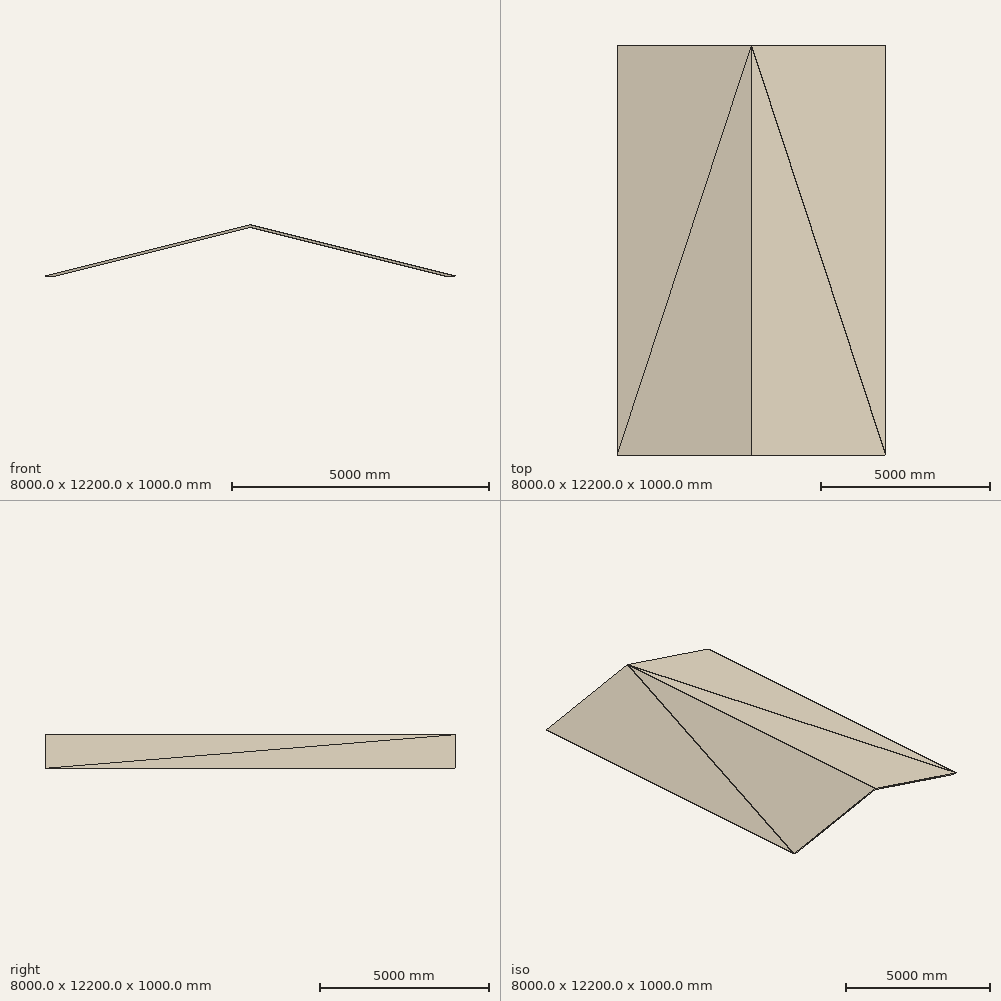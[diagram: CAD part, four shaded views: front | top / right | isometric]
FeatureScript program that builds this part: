
annotation { "Feature Type Name" : "Feature", "Feature Type Description" : "" }
export const myFeature = defineFeature(function(context is Context, id is Id, definition is map)
    precondition{}
    {
        {
            var Q0;
            Q0=qCreatedBy(makeId("Front.planeOp"),FACE);
            var sketch = newSketch(context, id + "F0", { "sketchPlane" : qUnion([Q0])});
            skLineSegment(sketch, "E0", {"start": v(0, 0) * mm, "end": v(8000, 0) * mm, "construction": true});
            skLineSegment(sketch, "E1", {"start": v(8000, 0) * mm, "end": v(4000, 1000) * mm});
            skLineSegment(sketch, "E2", {"start": v(4000, 1000) * mm, "end": v(0, 0) * mm});
            skLineSegment(sketch, "E3", {"start": v(0, 0) * mm, "end": v(206.16, 0) * mm});
            skLineSegment(sketch, "E4", {"start": v(206.16, 0) * mm, "end": v(4000, 948.46) * mm});
            skLineSegment(sketch, "E5", {"start": v(4000, 948.46) * mm, "end": v(7793.84, 0) * mm});
            skLineSegment(sketch, "E6", {"start": v(7793.84, 0) * mm, "end": v(8000, 0) * mm});
            skSolve(sketch);
        }
        {
            var Q0;
            Q0 = qSketchRegion(id + "F0", true);
            extrude(context, id + "F1", {"entities" : qUnion([Q0]), "depth" : 12200 * mm, "offsetDistance" : 25 * mm});
        }
    });
